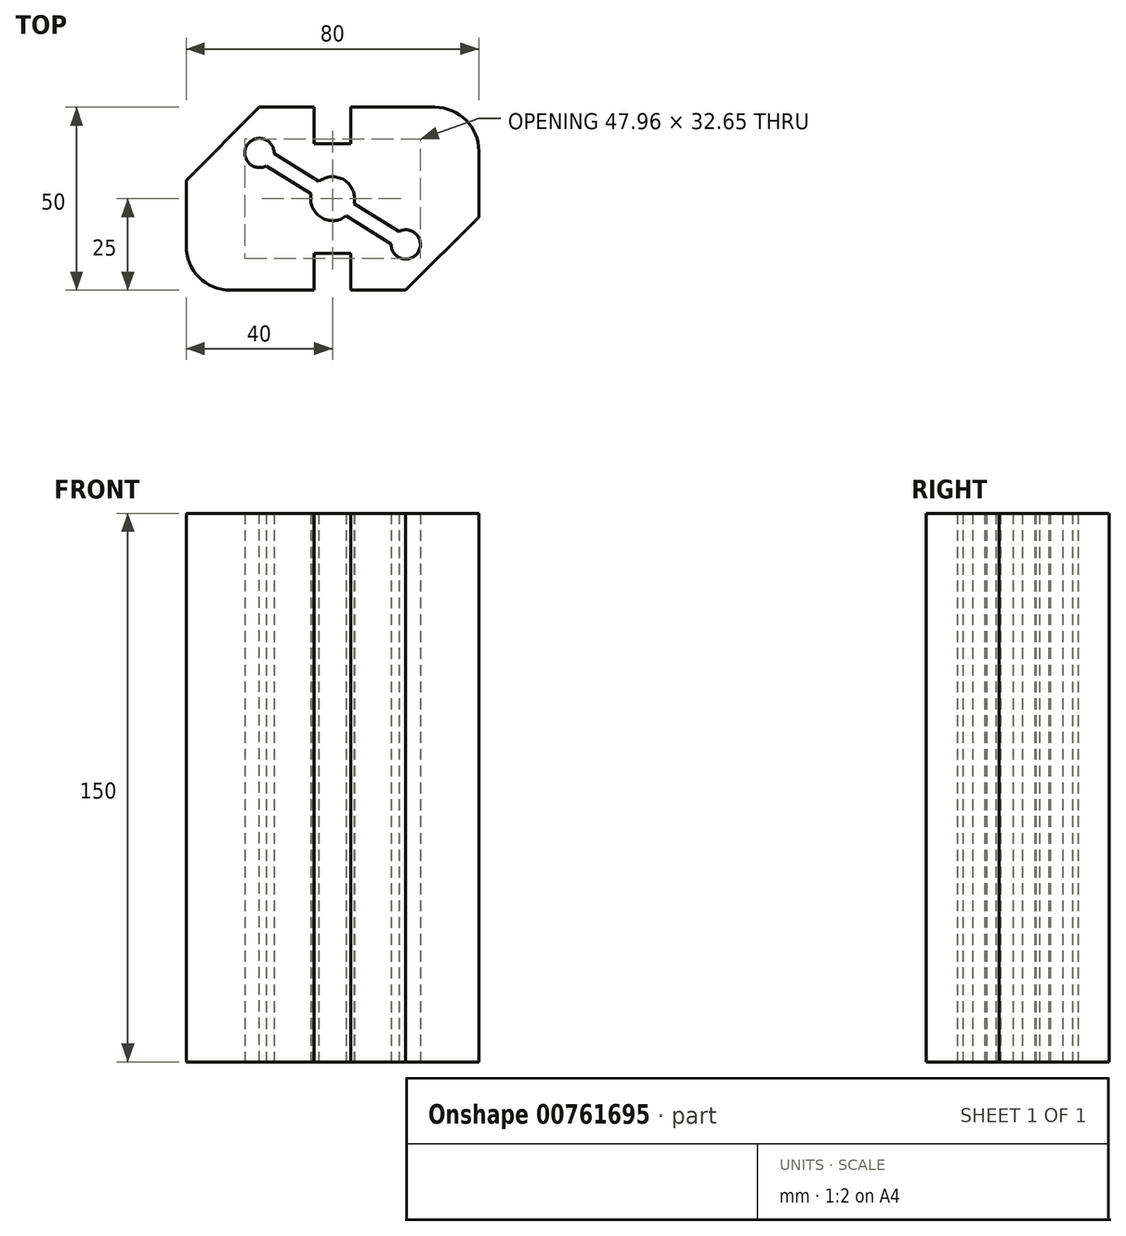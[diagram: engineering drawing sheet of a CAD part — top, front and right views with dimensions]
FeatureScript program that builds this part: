
annotation { "Feature Type Name" : "Feature", "Feature Type Description" : "" }
export const myFeature = defineFeature(function(context is Context, id is Id, definition is map)
    precondition{}
    {
        {
            var Q0;
            Q0=qCreatedBy(makeId("Top.planeOp"),FACE);
            var sketch = newSketch(context, id + "F0", { "sketchPlane" : qUnion([Q0])});
            skLineSegment(sketch, "E0.bottom", {"start": v(28, 25) * mm, "end": v(5, 25) * mm});
            skLineSegment(sketch, "E0.top", {"start": v(40, -25) * mm, "end": v(5, -25) * mm});
            skLineSegment(sketch, "E0.left", {"start": v(40, 13) * mm, "end": v(40, -25) * mm});
            skLineSegment(sketch, "E0.right", {"start": v(-40, 25) * mm, "end": v(-40, -13) * mm});
            skArc(sketch, "E1", {"start": v(-16, 12.36) * mm, "mid": v(-23.4, 14.62) * mm, "end": v(-18.12, 8.97) * mm});
            skArc(sketch, "E2", {"start": v(16, -12.36) * mm, "mid": v(23.4, -14.62) * mm, "end": v(18.12, -8.97) * mm});
            skLineSegment(sketch, "E3.bottom", {"start": v(-5, -15) * mm, "end": v(5, -15) * mm});
            skLineSegment(sketch, "E3.left", {"start": v(-5, -15) * mm, "end": v(-5, -25) * mm});
            skLineSegment(sketch, "E3.right", {"start": v(5, -15) * mm, "end": v(5, -25) * mm});
            skPoint(sketch, "E3.middle", {"position": v(0, -25) * mm});
            skLineSegment(sketch, "E4.bottom", {"start": v(-5, 15) * mm, "end": v(5, 15) * mm});
            skLineSegment(sketch, "E4.left", {"start": v(-5, 15) * mm, "end": v(-5, 25) * mm});
            skLineSegment(sketch, "E4.right", {"start": v(5, 15) * mm, "end": v(5, 25) * mm});
            skPoint(sketch, "E4.middle", {"position": v(0, 25) * mm});
            skPoint(sketch, "E5.orphan", {"position": v(5, -35) * mm});
            skPoint(sketch, "E6.orphan", {"position": v(-5, -35) * mm});
            skPoint(sketch, "E4.top.start.orphan", {"position": v(-5, 35) * mm});
            skPoint(sketch, "E7.orphan", {"position": v(5, 35) * mm});
            skLineSegment(sketch, "E8.trimOffspring", {"start": v(-5, 25) * mm, "end": v(-40, 25) * mm});
            skLineSegment(sketch, "E9.trimOffspring", {"start": v(-5, -25) * mm, "end": v(-28, -25) * mm});
            skPoint(sketch, "E10.visualSharp", {"position": v(40, 25) * mm});
            skArc(sketch, "E10.filletArc", {"start": v(40, 13) * mm, "mid": v(36.49, 21.49) * mm, "end": v(28, 25) * mm});
            skPoint(sketch, "E11.visualSharp", {"position": v(-40, -25) * mm});
            skArc(sketch, "E11.filletArc", {"start": v(-40, -13) * mm, "mid": v(-36.49, -21.49) * mm, "end": v(-28, -25) * mm});
            skArc(sketch, "E12", {"start": v(-5.86, 1.3) * mm, "mid": v(-3.18, -5.09) * mm, "end": v(3.74, -4.7) * mm});
            skLineSegment(sketch, "E13", {"start": v(16.6, -10.38) * mm, "end": v(-23.4, 14.62) * mm, "construction": true});
            skLineSegment(sketch, "E14.0", {"start": v(18.12, -8.97) * mm, "end": v(5.86, -1.3) * mm});
            skLineSegment(sketch, "E15.0", {"start": v(16, -12.36) * mm, "end": v(3.74, -4.7) * mm});
            skArc(sketch, "E16.trimOffspring", {"start": v(5.86, -1.3) * mm, "mid": v(3.18, 5.09) * mm, "end": v(-3.74, 4.7) * mm});
            skLineSegment(sketch, "E17.trimOffspring", {"start": v(-3.74, 4.7) * mm, "end": v(-16, 12.36) * mm});
            skLineSegment(sketch, "E18.trimOffspring", {"start": v(-5.86, 1.3) * mm, "end": v(-18.12, 8.97) * mm});
            skSolve(sketch);
        }
        {
            var Q0;
            Q0=makeQuery(id+"F0.imprint","IMPRINT",FACE,{"disambiguationData":[TD([[makeQuery(id+"F0.imprint","IMPRINT",EDGE,{"derivedFrom":sQuery(id+"F0.wireOp",EDGE,"E0.bottom")}),1.0]])]});
            extrude(context, id + "F1", {"entities" : qUnion([Q0]), "depth" : 150 * mm, "offsetDistance" : 25 * mm});
        }
        {
            var Q0;
            Q0=makeQuery(id+"F1.opExtrude","SWEPT_EDGE",EDGE,{"disambiguationData":[OSD([sQuery(id+"F0.wireOp",EDGE,"E0.right"),sQuery(id+"F0.wireOp",EDGE,"E8.trimOffspring")])]});
            var Q1;
            Q1=makeQuery(id+"F1.opExtrude","SWEPT_EDGE",EDGE,{"disambiguationData":[OSD([sQuery(id+"F0.wireOp",EDGE,"E0.top"),sQuery(id+"F0.wireOp",EDGE,"E0.left")])]});
            chamfer(context, id + "F2", {"entities" : qUnion([Q0, Q1]), "width" : 20 * mm, "tangentPropagation" : true});
        }
    });
